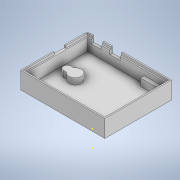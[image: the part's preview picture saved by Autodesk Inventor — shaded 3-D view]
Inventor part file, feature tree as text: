
AUTODESK INVENTOR PART (.ipt)
format: ipt  version: 2022 (Build 260153000, 153)  size: 244,736 bytes
history: native  units: in
note: dims shown in document units (in); Inventor stores cm internally (conversion verified against a paired STEP export)
features: sketch x8, extrude x8, fillet x1
ambient origin geometry x8: Origin, YZ Plane, XZ Plane, XY Plane, X Axis, Y Axis, Z Axis, Center Point
bodies: Solid1 (feature_tree)
feature tree (17):
  sketch  "Sketch1"  dims[d2=0.5512in d3=0.0in d6=0.0787in]
  extrude  "Extrusion1"  Depth=0.0787in
  sketch  "Sketch3"  dims[d8=0.0787in d13=0.4724in d14=0.0in]
  extrude  "Extrusion2"  Depth=0.4724in TaperAngle=0.0deg
  extrude  "Extrusion5"  Depth=0.5906in
  extrude  "Extrusion7"  Depth=0.2362in TaperAngle=0.0deg
  extrude  "Extrusion8"  Depth=0.0787in TaperAngle=0.0deg
  extrude  "Extrusion9"  Depth=0.0394in
  extrude  "Extrusion10"  Depth=0.0787in
  fillet  "Fillet8"  Radius=0.0787in
  extrude  "Extrusion11"  Depth=0.315in
  sketch  "Sketch4"  dims[d55=0.1181in d56=0.5906in]
  sketch  "Sketch10"  dims[d60=0.5906in d64=0.2362in d65=0.0in]
  sketch  "Sketch12"  dims[d79=0.2362in d80=0.0in d88=0.0787in d89=0.0in]
  sketch  "Sketch15"  dims[d94=0.0394in d95=0.0394in d96=0.0394in d97=0.0394in d99=0.0394in]
  sketch  "Sketch16"  dims[d101=0.0394in d102=0.0787in d104=0.0787in]
  sketch  "Sketch17"  dims[d108=0.1181in d118=0.315in d125=0.3937in d126=0.0in d127=0.3346in d128=0.3346in d131=1.126in d132=0.5315in d133=0.3937in d134=0.0in d140=1.0933in d141=0.3543in d143=0.1969in d145=0.1181in d148=0.1969in d149=0.2362in d150=0.1575in d151=2.6772in d152=2.126in d153=0.0787in d154=0.0787in d155=0.0in d158=0.315in d159=0.2559in d160=0.1575in d162=0.1969in d163=0.0in d40=0.0197in d41=0.0344in d42=0.0197in d43=0.0344in d66=0.0197in d67=0.0344in d74=0.0197in d75=0.0344in d76=0.0197in d77=0.0344in d115=0.0in d116=0.0in d117=0.0in d135=0.0197in d136=0.0344in d137=0.0197in d138=0.0344in]
